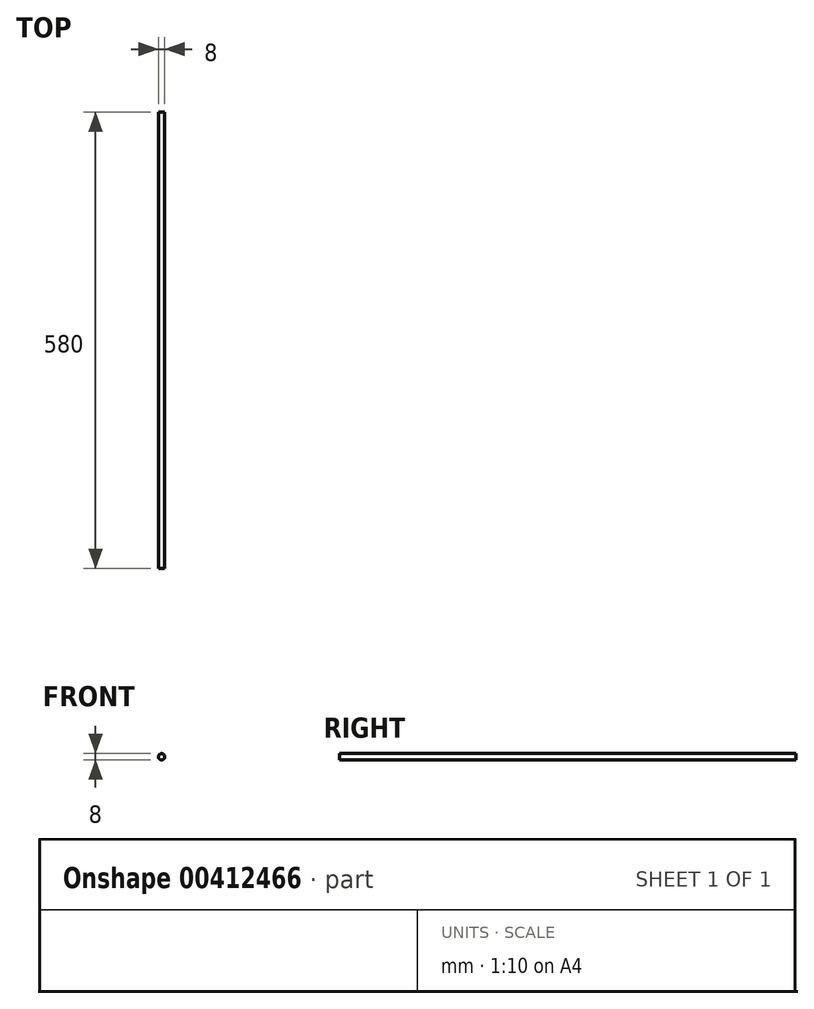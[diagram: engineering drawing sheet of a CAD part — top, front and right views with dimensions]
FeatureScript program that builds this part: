
annotation { "Feature Type Name" : "Feature", "Feature Type Description" : "" }
export const myFeature = defineFeature(function(context is Context, id is Id, definition is map)
    precondition{}
    {
        {
            var Q0;
            Q0=qCreatedBy(makeId("Front.planeOp"),FACE);
            var sketch = newSketch(context, id + "F0", { "sketchPlane" : qUnion([Q0])});
            skCircle(sketch, "E0", {"center": v(0, 0) * mm, "radius": 4 * mm});
            skSolve(sketch);
        }
        {
            var Q0;
            Q0=qSketchRegion(id+"F0",true);
            extrude(context, id + "F1", {"entities" : qUnion([Q0]), "endBound" : BoundingType.SYMMETRIC, "depth" : 580 * mm});
        }
    });
